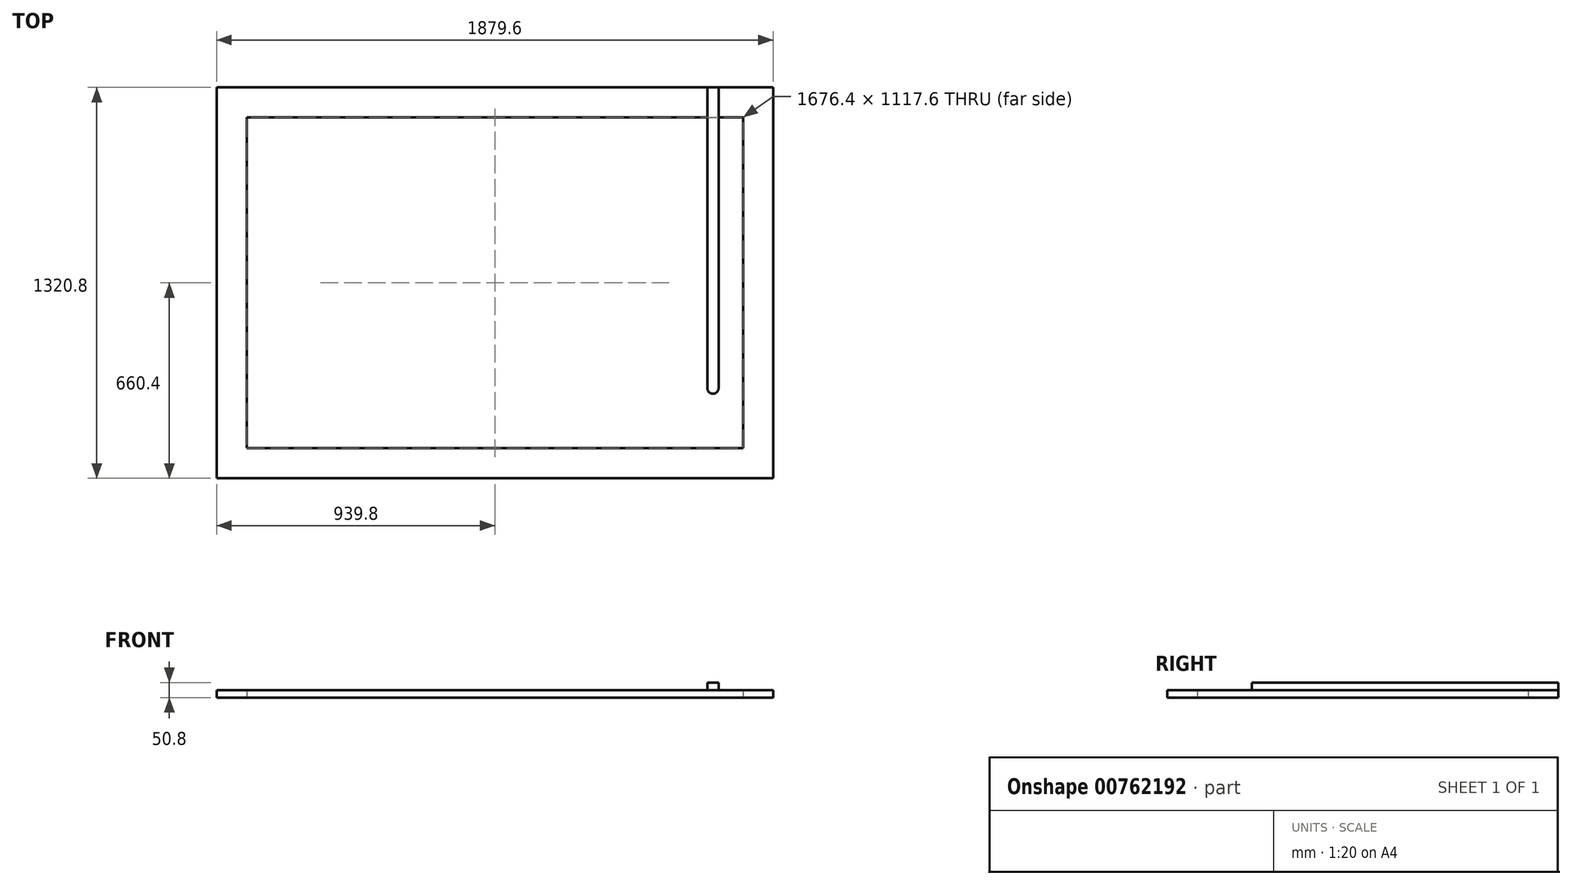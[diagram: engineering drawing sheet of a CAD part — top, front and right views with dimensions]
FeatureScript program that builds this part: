
annotation { "Feature Type Name" : "Feature", "Feature Type Description" : "" }
export const myFeature = defineFeature(function(context is Context, id is Id, definition is map)
    precondition{}
    {
        {
            var Q0;
            Q0=qCreatedBy(makeId("Top.planeOp"),FACE);
            var sketch = newSketch(context, id + "F0", { "sketchPlane" : qUnion([Q0])});
            skLineSegment(sketch, "E0.bottom", {"start": v(0, 0) * mm, "end": v(1879.6, 0) * mm});
            skLineSegment(sketch, "E0.top", {"start": v(0, -1320.8) * mm, "end": v(1879.6, -1320.8) * mm});
            skLineSegment(sketch, "E0.left", {"start": v(0, 0) * mm, "end": v(0, -1320.8) * mm});
            skLineSegment(sketch, "E0.right", {"start": v(1879.6, 0) * mm, "end": v(1879.6, -1320.8) * mm});
            skLineSegment(sketch, "E1.bottom", {"start": v(101.6, -101.6) * mm, "end": v(1778, -101.6) * mm});
            skLineSegment(sketch, "E1.top", {"start": v(101.6, -1219.2) * mm, "end": v(1778, -1219.2) * mm});
            skLineSegment(sketch, "E1.left", {"start": v(101.6, -101.6) * mm, "end": v(101.6, -1219.2) * mm});
            skLineSegment(sketch, "E1.right", {"start": v(1778, -101.6) * mm, "end": v(1778, -1219.2) * mm});
            skSolve(sketch);
        }
        {
            var Q0;
            Q0 = qSketchRegion(id + "F0", true);
            extrude(context, id + "F1", {"entities" : qUnion([Q0]), "depth" : 25.4 * mm, "offsetDistance" : 25.4 * mm});
        }
        {
            var Q0;
            Q0=makeQuery(id+"F1.opExtrude","CAP_FACE",FACE,{"disambiguationData":[OSD([sQuery(id+"F0.wireOp",EDGE,"E0.bottom"),sQuery(id+"F0.wireOp",EDGE,"E0.top"),sQuery(id+"F0.wireOp",EDGE,"E0.left"),sQuery(id+"F0.wireOp",EDGE,"E0.right"),sQuery(id+"F0.wireOp",EDGE,"E1.bottom"),sQuery(id+"F0.wireOp",EDGE,"E1.top"),sQuery(id+"F0.wireOp",EDGE,"E1.left"),sQuery(id+"F0.wireOp",EDGE,"E1.right")])],"isStart":false});
            var sketch = newSketch(context, id + "F2", { "sketchPlane" : qUnion([Q0])});
            skLineSegment(sketch, "E2.bottom", {"start": v(1657.35, 0) * mm, "end": v(1695.45, 0) * mm});
            skLineSegment(sketch, "E2.top", {"start": v(1657.35, -1016) * mm, "end": v(1695.45, -1016) * mm});
            skLineSegment(sketch, "E2.left", {"start": v(1657.35, 0) * mm, "end": v(1657.35, -1016) * mm});
            skLineSegment(sketch, "E2.right", {"start": v(1695.45, 0) * mm, "end": v(1695.45, -1016) * mm});
            skCircle(sketch, "E3", {"center": v(1676.4, -1016) * mm, "radius": 19.05 * mm});
            skSolve(sketch);
        }
        {
            var Q0;
            Q0 = qSketchRegion(id + "F2", true);
            extrude(context, id + "F3", {"entities" : qUnion([Q0]), "depth" : 25.4 * mm, "offsetDistance" : 25.4 * mm});
        }
    });
